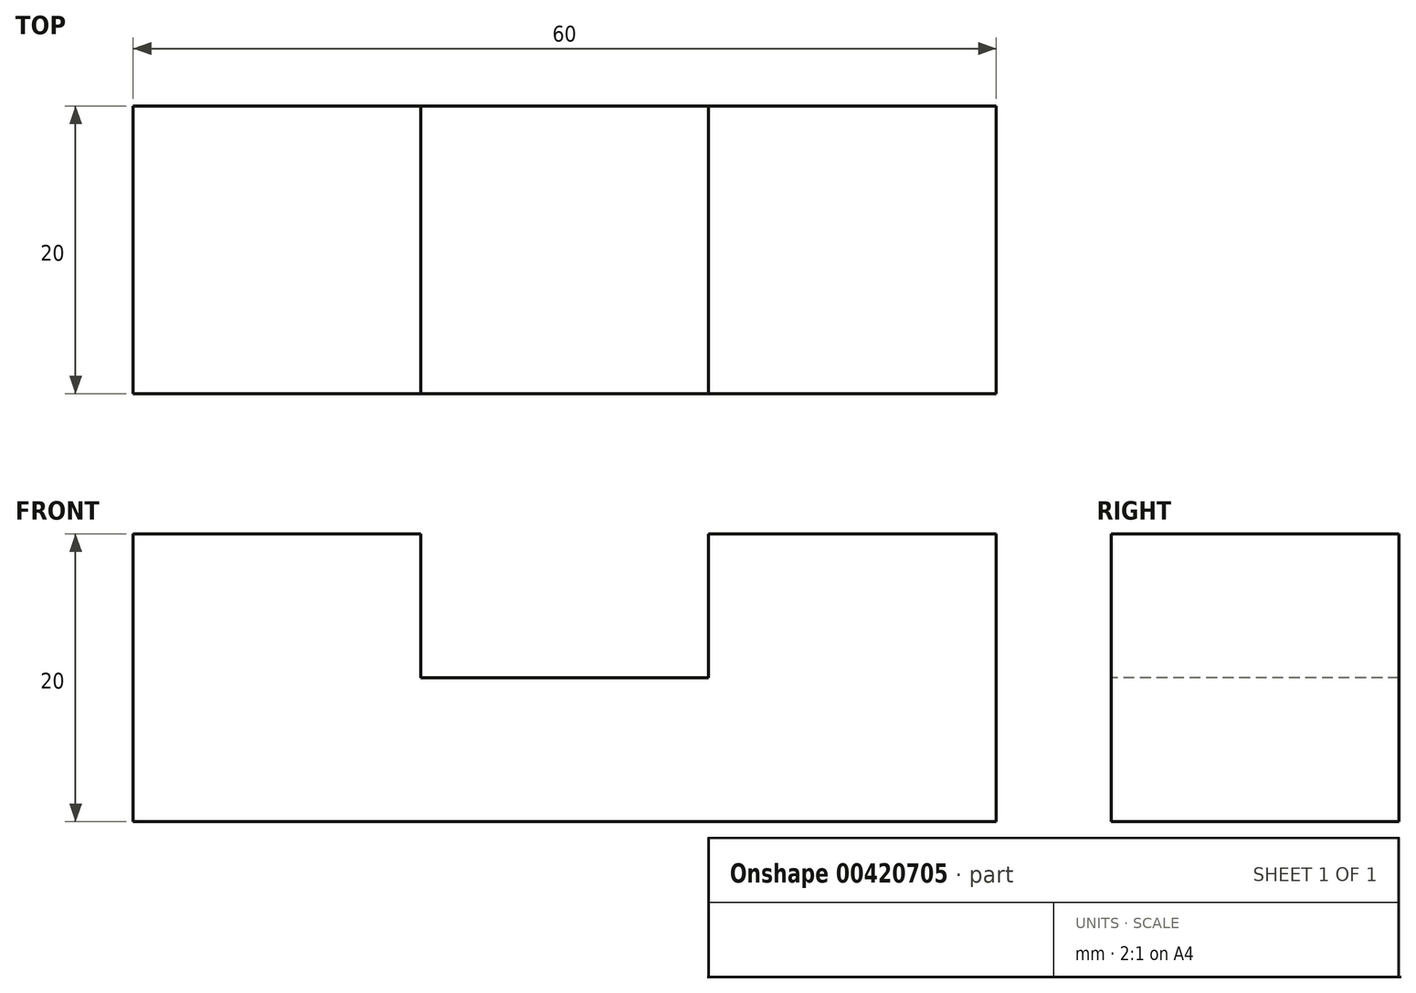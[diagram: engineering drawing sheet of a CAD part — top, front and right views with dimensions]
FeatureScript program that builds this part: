
annotation { "Feature Type Name" : "Feature", "Feature Type Description" : "" }
export const myFeature = defineFeature(function(context is Context, id is Id, definition is map)
    precondition{}
    {
        {
            var Q0;
            Q0=qCreatedBy(makeId("Right.planeOp"),FACE);
            var sketch = newSketch(context, id + "F0", { "sketchPlane" : qUnion([Q0])});
            skLineSegment(sketch, "E0.bottom", {"start": v(10, 10) * mm, "end": v(-10, 10) * mm});
            skLineSegment(sketch, "E0.top", {"start": v(10, -10) * mm, "end": v(-10, -10) * mm});
            skLineSegment(sketch, "E0.left", {"start": v(10, 10) * mm, "end": v(10, -10) * mm});
            skLineSegment(sketch, "E0.right", {"start": v(-10, 10) * mm, "end": v(-10, -10) * mm});
            skPoint(sketch, "E0.middle", {"position": v(0, 0) * mm});
            skSolve(sketch);
        }
        {
            var Q0;
            Q0 = qSketchRegion(id + "F0", true);
            extrude(context, id + "F1", {"entities" : qUnion([Q0]), "endBound" : BoundingType.SYMMETRIC, "depth" : 60 * mm});
        }
        {
            var Q0;
            Q0=makeQuery(id+"F1.opExtrude","SWEPT_FACE",FACE,{"disambiguationData":[OSD([sQuery(id+"F0.wireOp",EDGE,"E0.right")])]});
            var sketch = newSketch(context, id + "F2", { "sketchPlane" : qUnion([Q0])});
            skLineSegment(sketch, "E1.bottom", {"start": v(-10, 10) * mm, "end": v(10, 10) * mm});
            skLineSegment(sketch, "E1.top", {"start": v(-10, 0) * mm, "end": v(10, 0) * mm});
            skLineSegment(sketch, "E1.left", {"start": v(-10, 10) * mm, "end": v(-10, 0) * mm});
            skLineSegment(sketch, "E1.right", {"start": v(10, 10) * mm, "end": v(10, 0) * mm});
            skSolve(sketch);
        }
        {
            var Q0;
            Q0 = qSketchRegion(id + "F2", true);
            extrude(context, id + "F3", {"entities" : qUnion([Q0]), "operationType" : NewBodyOperationType.REMOVE, "oppositeDirection" : true, "depth" : 20 * mm});
        }
    });
